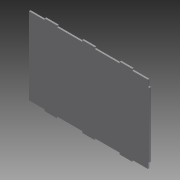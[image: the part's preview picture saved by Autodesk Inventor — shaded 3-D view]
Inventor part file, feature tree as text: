
AUTODESK INVENTOR PART (.ipt)
format: ipt  version: 2011 (Build 150239000, 239)  size: 124,928 bytes
history: native  units: in
note: dims shown in document units (in); Inventor stores cm internally (conversion verified against a paired STEP export)
features: extrude x3, sketch x3
ambient origin geometry x8: Origin, YZ Plane, XZ Plane, XY Plane, X Axis, Y Axis, Z Axis, Center Point
bodies: Solid1 (feature_tree)
feature tree (6):
  extrude  "Extrusion1"  Depth=12.35in
  extrude  "Extrusion2"  Depth=2.0in
  extrude  "Extrusion3"  Depth=2.0in
  sketch  "Sketch1"  dims[d0=19.0in d1=12.35in]
  sketch  "Sketch2"  dims[d2=2.5in d3=2.0in]
  sketch  "Sketch3"  dims[d4=4.0in d5=2.0in d6=4.0in d7=2.0in d8=2.5in d9=0.25in d10=0.25in d11=0.25in d12=0.0in d13=1.0in d14=10.35in d15=0.25in d16=0.0in d17=19.5in d18=0.0in]
